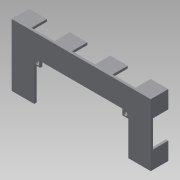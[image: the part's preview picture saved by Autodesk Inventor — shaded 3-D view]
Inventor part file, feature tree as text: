
AUTODESK INVENTOR PART (.ipt)
format: ipt  version: 2015 SP1 (Build 190203100, 203)  size: 150,528 bytes
history: native  units: mm
features: extrude x3, sketch x3, projected_geometry x1
ambient origin geometry x8: Origin, YZ Plane, XZ Plane, XY Plane, X Axis, Y Axis, Z Axis, Center Point
bodies: Solid1 (feature_tree)
feature tree (7):
  extrude  "Extrusion1"  Depth=15.0mm
  extrude  "Extrusion2"  Depth=88.597889mm
  extrude  "Extrusion3"  Depth=15.0mm
  sketch  "Sketch1"  dims[d0=3.0mm d1=0.0mm d3=15.0mm]
  sketch  "Sketch3"  dims[d4=2.0mm d5=88.597889mm]
  sketch  "Sketch5"  dims[d6=19.532667mm d7=15.0mm d8=19.532667mm d9=15.0mm d10=2.0mm d11=15.0mm d12=2.0mm d13=13.0mm d14=0.0mm d15=2.0mm d16=2.0mm d17=1.0mm d18=0.0mm]
  projected_geometry  "Projected Loop2"
